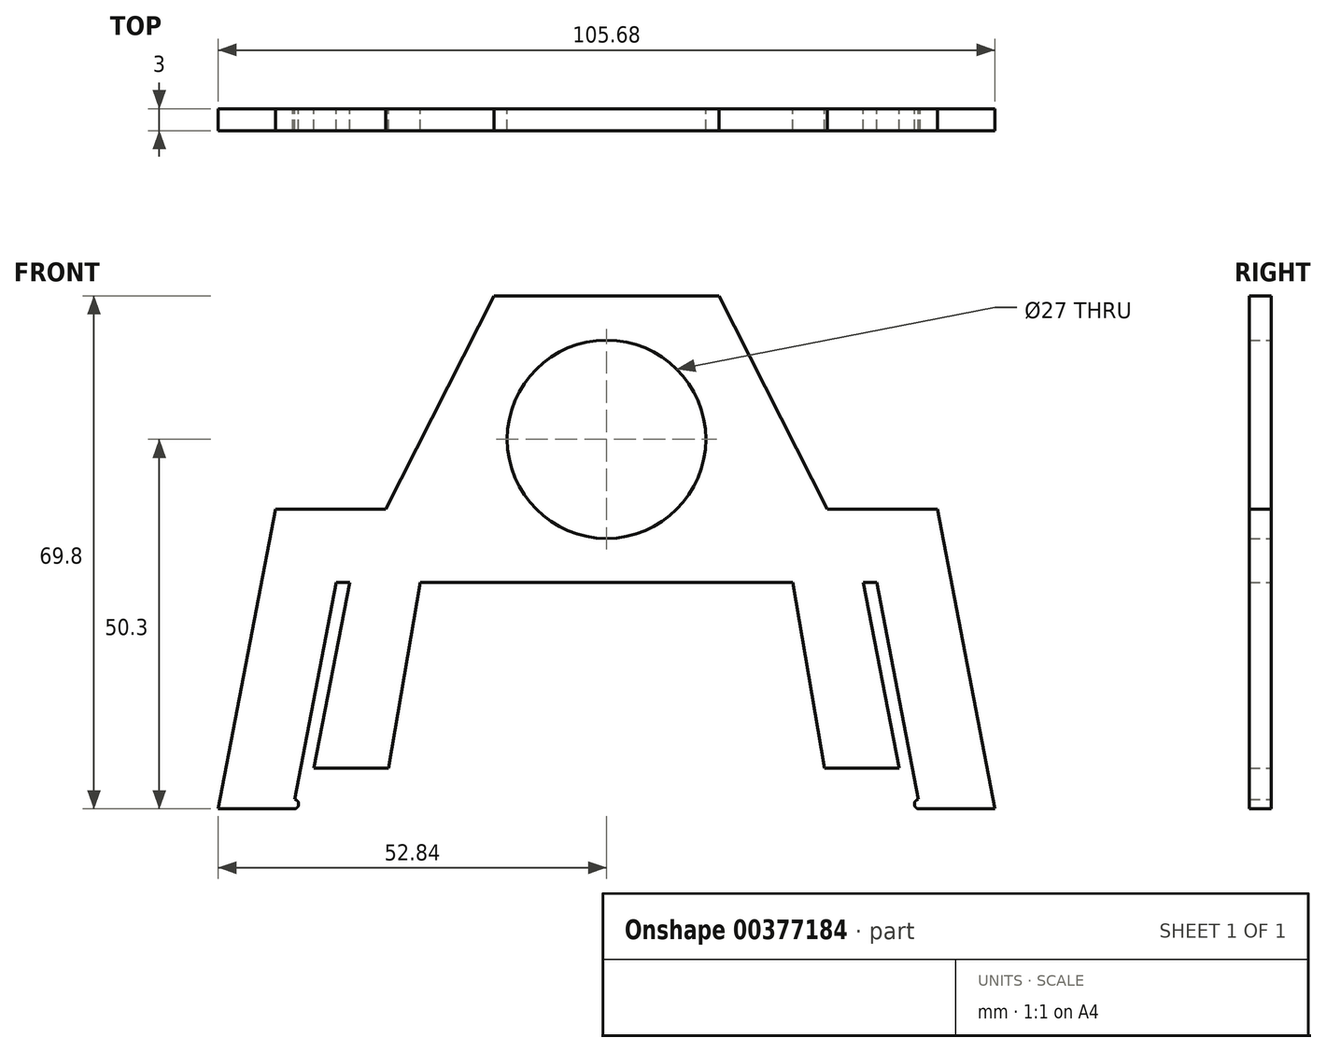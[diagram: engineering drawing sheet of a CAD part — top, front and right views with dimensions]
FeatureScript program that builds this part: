
annotation { "Feature Type Name" : "Feature", "Feature Type Description" : "" }
export const myFeature = defineFeature(function(context is Context, id is Id, definition is map)
    precondition{}
    {
        {
            var Q0;
            Q0=qCreatedBy(makeId("Front.planeOp"),FACE);
            var sketch = newSketch(context, id + "F0", { "sketchPlane" : qUnion([Q0])});
            skLineSegment(sketch, "E0", {"start": v(34.94, 0) * mm, "end": v(39.8, -25.28) * mm});
            skLineSegment(sketch, "E1", {"start": v(39.8, -25.28) * mm, "end": v(29.66, -25.28) * mm});
            skLineSegment(sketch, "E2", {"start": v(29.66, -25.28) * mm, "end": v(25.31, 0) * mm});
            skLineSegment(sketch, "E3", {"start": v(34.94, 0) * mm, "end": v(36.74, 0) * mm});
            skLineSegment(sketch, "E4", {"start": v(36.74, 0) * mm, "end": v(42.66, -30.79) * mm});
            skLineSegment(sketch, "E5", {"start": v(42.66, -30.79) * mm, "end": v(52.84, -30.79) * mm});
            skLineSegment(sketch, "E6", {"start": v(52.84, -30.79) * mm, "end": v(45, 10) * mm});
            skLineSegment(sketch, "E7", {"start": v(45, 10) * mm, "end": v(0, 10) * mm});
            skLineSegment(sketch, "E8", {"start": v(25.31, 0) * mm, "end": v(0, 0) * mm});
            skLineSegment(sketch, "E9.MirrorCS", {"start": v(-34.94, 0) * mm, "end": v(-36.74, 0) * mm});
            skLineSegment(sketch, "E10.MirrorCS", {"start": v(-25.31, 0) * mm, "end": v(0, 0) * mm});
            skLineSegment(sketch, "E11.MirrorCS", {"start": v(-36.74, 0) * mm, "end": v(-42.66, -30.79) * mm});
            skLineSegment(sketch, "E12.MirrorCS", {"start": v(-45, 10) * mm, "end": v(0, 10) * mm});
            skLineSegment(sketch, "E13.MirrorCS", {"start": v(-34.94, 0) * mm, "end": v(-39.8, -25.28) * mm});
            skLineSegment(sketch, "E14.MirrorCS", {"start": v(-52.84, -30.79) * mm, "end": v(-45, 10) * mm});
            skLineSegment(sketch, "E15.MirrorCS", {"start": v(-39.8, -25.28) * mm, "end": v(-29.66, -25.28) * mm});
            skLineSegment(sketch, "E16.MirrorCS", {"start": v(-29.66, -25.28) * mm, "end": v(-25.31, 0) * mm});
            skLineSegment(sketch, "E17.MirrorCS", {"start": v(-42.66, -30.79) * mm, "end": v(-52.84, -30.79) * mm});
            skLineSegment(sketch, "E18", {"start": v(30.03, 10) * mm, "end": v(15.3, 39) * mm});
            skLineSegment(sketch, "E19", {"start": v(15.3, 39) * mm, "end": v(0, 39) * mm});
            skLineSegment(sketch, "E20.MirrorCS", {"start": v(-15.3, 39) * mm, "end": v(0, 39) * mm});
            skLineSegment(sketch, "E21.MirrorCS", {"start": v(-30.03, 10) * mm, "end": v(-15.3, 39) * mm});
            skCircle(sketch, "E22", {"center": v(0, 19.5) * mm, "radius": 13.5 * mm});
            skLineSegment(sketch, "E23", {"start": v(0, 19.5) * mm, "end": v(0, 10) * mm});
            skArc(sketch, "E24", {"start": v(-42.66, -30.79) * mm, "mid": v(-41.9, -30.27) * mm, "end": v(-42.42, -29.51) * mm});
            skArc(sketch, "E25.MirrorCS", {"start": v(42.66, -30.79) * mm, "mid": v(41.9, -30.27) * mm, "end": v(42.42, -29.51) * mm});
            skSolve(sketch);
        }
        {
            var Q0;
            Q0=qSketchRegion(id+"F0",true);
            extrude(context, id + "F1", {"entities" : qUnion([Q0]), "depth" : 3 * mm});
        }
    });
